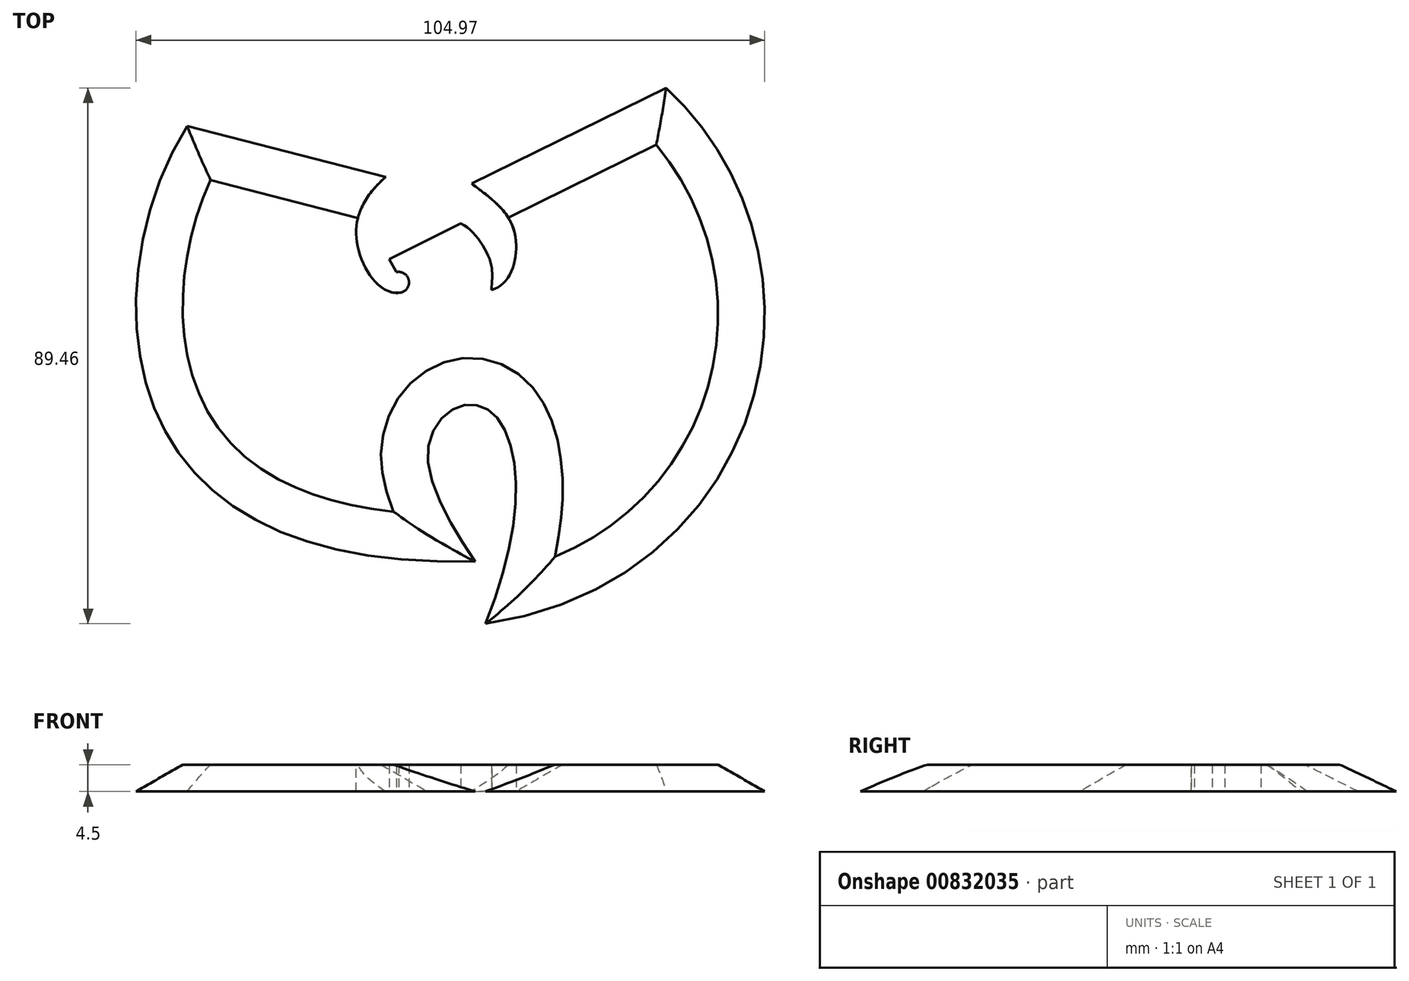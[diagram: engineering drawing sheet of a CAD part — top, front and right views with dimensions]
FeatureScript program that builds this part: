
annotation { "Feature Type Name" : "Feature", "Feature Type Description" : "" }
export const myFeature = defineFeature(function(context is Context, id is Id, definition is map)
    precondition{}
    {
        {
            var Q0;
            Q0=qCreatedBy(makeId("Top.planeOp"),FACE);
            var sketch = newSketch(context, id + "F0", { "sketchPlane" : qUnion([Q0])});
            skArc(sketch, "E0", {"start": v(-5.72, 6.83) * mm, "mid": v(-4.56, 8.1) * mm, "end": v(-5.94, 9.14) * mm});
            skLineSegment(sketch, "E1", {"start": v(-5.94, 9.14) * mm, "end": v(-6.76, 10.56) * mm});
            skLineSegment(sketch, "E2", {"start": v(-6.76, 10.56) * mm, "end": v(1.2, 14.57) * mm});
            skFitSpline(sketch, "E3", {"points": [v(1.2, 14.57) * mm, v(4.53, 10.2) * mm, v(4.61, 7.15) * mm], "startDerivative": vector(8.3, -4.32) * mm, "endDerivative": vector(-0.33, -8.29) * mm});
            skFitSpline(sketch, "E4", {"points": [v(4.61, 7.15) * mm, v(7.2, 13.54) * mm, v(2.42, 19) * mm], "startDerivative": vector(14.39, 3.3) * mm, "endDerivative": vector(-13.13, 10.23) * mm});
            skLineSegment(sketch, "E5", {"start": v(2.42, 19) * mm, "end": v(24.06, 29.64) * mm});
            skFitSpline(sketch, "E6", {"points": [v(24.06, 29.64) * mm, v(34.76, 0) * mm, v(3.95, -30) * mm], "startDerivative": vector(49.8, -45.42) * mm, "endDerivative": vector(-106.2, -15.94) * mm});
            skFitSpline(sketch, "E7", {"points": [v(3.95, -30) * mm, v(7.32, -13.65) * mm, v(4.73, -6.53) * mm, v(0.85, -5.89) * mm, v(-2.48, -10.97) * mm, v(2.79, -23.07) * mm], "startDerivative": vector(25.96, 64.8) * mm, "endDerivative": vector(29.7, -44.79) * mm});
            skFitSpline(sketch, "E8", {"points": [v(2.79, -23.07) * mm, v(-24.84, -16.42) * mm, v(-34.54, 0) * mm, v(-29.26, 25.4) * mm], "startDerivative": vector(-98.98, -2.11) * mm, "endDerivative": vector(41.71, 66.36) * mm});
            skLineSegment(sketch, "E9", {"start": v(-29.26, 25.4) * mm, "end": v(-7.16, 19.73) * mm});
            skFitSpline(sketch, "E10", {"points": [v(-7.16, 19.73) * mm, v(-10.3, 12.15) * mm, v(-5.72, 6.83) * mm], "startDerivative": vector(-15.48, -13.88) * mm, "endDerivative": vector(14.2, 0.78) * mm});
            skCircle(sketch, "E11", {"center": v(20.53, 3.96) * mm, "radius": 11 * mm});
            skSolve(sketch);
        }
        {
            var Q0;
            Q0=makeQuery(id+"F0.imprint","IMPRINT",FACE,{"disambiguationData":[TD([[makeQuery(id+"F0.imprint","IMPRINT",EDGE,{"derivedFrom":sQuery(id+"F0.wireOp",EDGE,"E0")}),-1.0]])]});
            var Q1;
            Q1=makeQuery(id+"F0.imprint","IMPRINT",FACE,{"disambiguationData":[TD([[makeQuery(id+"F0.imprint","IMPRINT",EDGE,{"derivedFrom":sQuery(id+"F0.wireOp",EDGE,"E11")}),1.0]])]});
            extrude(context, id + "F1", {"entities" : qUnion([Q0, Q1]), "endBound" : BoundingType.SYMMETRIC, "offsetDistance" : 25 * mm, "depth" : 3 * mm});
        }
        {
            var Q0;
            Q0=makeQuery(id+"F1.opExtrude","SWEPT_BODY",BODY,{"disambiguationData":[OSD([sQuery(id+"F0.wireOp",EDGE,"E0"),sQuery(id+"F0.wireOp",EDGE,"E1"),sQuery(id+"F0.wireOp",EDGE,"E2"),sQuery(id+"F0.wireOp",EDGE,"E3"),sQuery(id+"F0.wireOp",EDGE,"E4"),sQuery(id+"F0.wireOp",EDGE,"E5"),sQuery(id+"F0.wireOp",EDGE,"E6"),sQuery(id+"F0.wireOp",EDGE,"E7"),sQuery(id+"F0.wireOp",EDGE,"E8"),sQuery(id+"F0.wireOp",EDGE,"E9"),sQuery(id+"F0.wireOp",EDGE,"E10")])]});
            var Q1;
            Q1=qCreatedBy(makeId("Origin.pointOp"),VERTEX);
            transform(context, id + "F2", {"entities" : qUnion([Q0]), "transformType" : TransformType.SCALE_UNIFORMLY, "scale" : 1.5, "scalePoint" : qUnion([Q1]), "makeCopy" : false});
        }
        {
            var Q0;
            Q0=makeQuery(id+"F1.opExtrude","CAP_EDGE",EDGE,{"disambiguationData":[OSD([sQuery(id+"F0.wireOp",EDGE,"E8")])],"isStart":false});
            var Q1;
            Q1=makeQuery(id+"F1.opExtrude","CAP_EDGE",EDGE,{"disambiguationData":[OSD([sQuery(id+"F0.wireOp",EDGE,"E9")])],"isStart":false});
            var Q2;
            Q2=makeQuery(id+"F1.opExtrude","CAP_EDGE",EDGE,{"disambiguationData":[OSD([sQuery(id+"F0.wireOp",EDGE,"E5")])],"isStart":false});
            var Q3;
            Q3=makeQuery(id+"F1.opExtrude","CAP_EDGE",EDGE,{"disambiguationData":[OSD([sQuery(id+"F0.wireOp",EDGE,"E6")])],"isStart":false});
            var Q4;
            Q4=makeQuery(id+"F1.opExtrude","CAP_EDGE",EDGE,{"disambiguationData":[OSD([sQuery(id+"F0.wireOp",EDGE,"E7")])],"isStart":false});
            chamfer(context, id + "F3", {"entities" : qUnion([Q0, Q1, Q2, Q3, Q4]), "chamferType" : ChamferType.OFFSET_ANGLE, "width" : 4.5 * mm, "oppositeDirection" : false, "angle" : 60 * degree, "tangentPropagation" : true});
        }
    });
